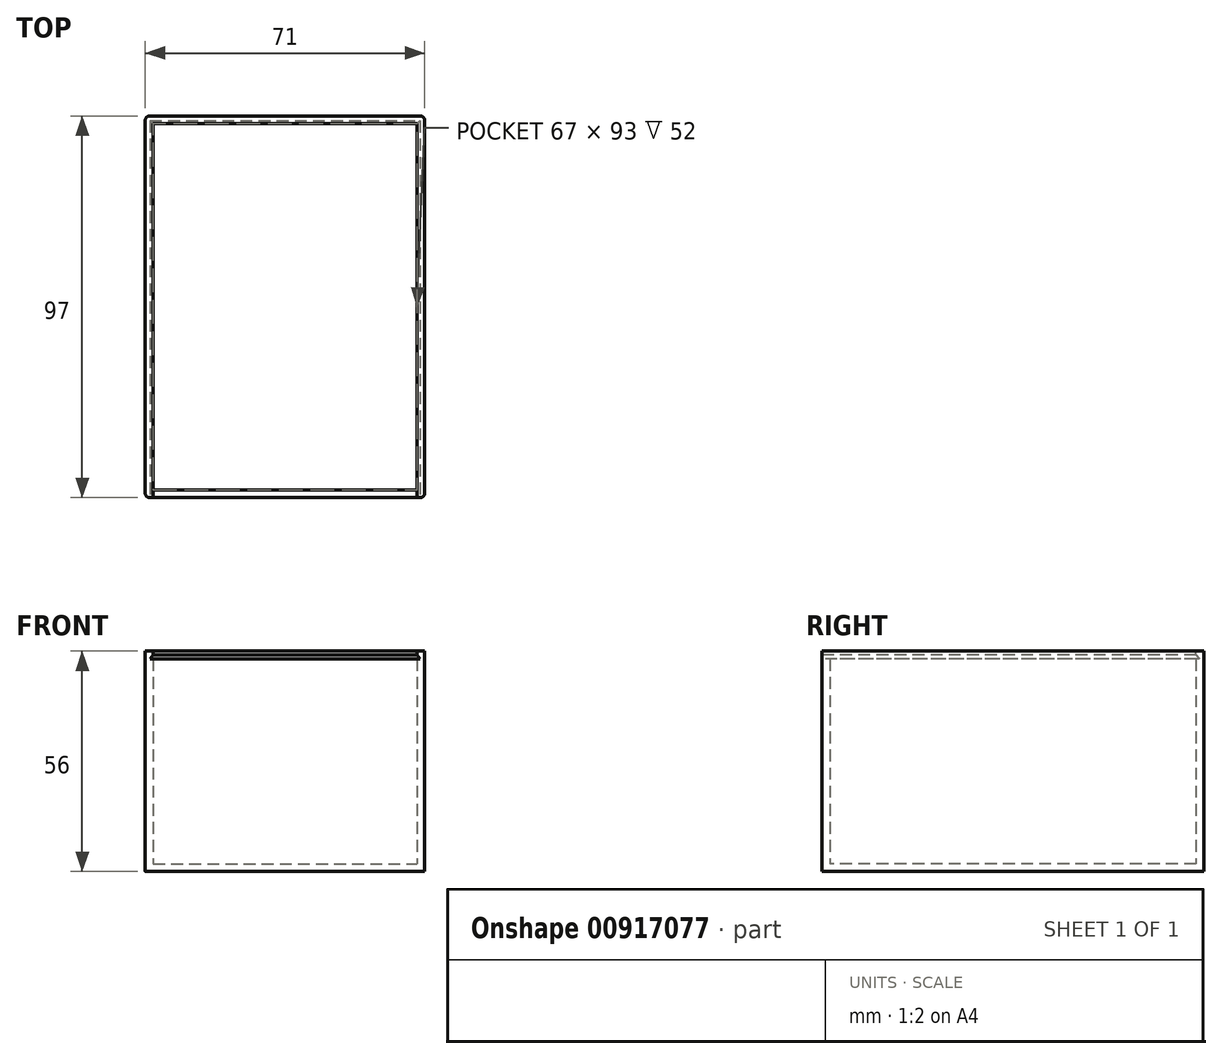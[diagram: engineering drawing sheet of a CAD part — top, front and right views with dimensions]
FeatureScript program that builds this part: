
annotation { "Feature Type Name" : "Feature", "Feature Type Description" : "" }
export const myFeature = defineFeature(function(context is Context, id is Id, definition is map)
    precondition{}
    {
        {
            var Q0;
            Q0=qCreatedBy(makeId("Front.planeOp"),FACE);
            var sketch = newSketch(context, id + "F0", { "sketchPlane" : qUnion([Q0])});
            skLineSegment(sketch, "E0.bottom", {"start": v(0, 0) * mm, "end": v(71, 0) * mm});
            skLineSegment(sketch, "E0.top", {"start": v(0, -54) * mm, "end": v(71, -54) * mm});
            skLineSegment(sketch, "E0.left", {"start": v(0, 0) * mm, "end": v(0, -54) * mm});
            skLineSegment(sketch, "E0.right", {"start": v(71, 0) * mm, "end": v(71, -54) * mm});
            skSolve(sketch);
        }
        {
            var Q0;
            Q0=qSketchRegion(id+"F0",true);
            extrude(context, id + "F1", {"entities" : qUnion([Q0]), "oppositeDirection" : true, "depth" : 97 * mm, "offsetDistance" : 25 * mm});
        }
        {
            var Q0;
            Q0=makeQuery(id+"F1.opExtrude","SWEPT_FACE",FACE,{"disambiguationData":[OSD([sQuery(id+"F0.wireOp",EDGE,"E0.bottom")])]});
            shell(context, id + "F2", {"entities" : qUnion([Q0]), "thickness" : 2 * mm});
        }
        {
            var Q0;
            Q0=makeQuery(id+"F1.opExtrude","CAP_FACE",FACE,{"disambiguationData":[OSD([sQuery(id+"F0.wireOp",EDGE,"E0.bottom"),sQuery(id+"F0.wireOp",EDGE,"E0.top"),sQuery(id+"F0.wireOp",EDGE,"E0.left"),sQuery(id+"F0.wireOp",EDGE,"E0.right")])],"isStart":true});
            var sketch = newSketch(context, id + "F3", { "sketchPlane" : qUnion([Q0])});
            skLineSegment(sketch, "E1", {"start": v(0, 0) * mm, "end": v(0, 2) * mm});
            skLineSegment(sketch, "E2", {"start": v(0, 2) * mm, "end": v(2, 2) * mm});
            skLineSegment(sketch, "E3", {"start": v(2, 2) * mm, "end": v(2, 1) * mm});
            skLineSegment(sketch, "E4", {"start": v(1.2, 0) * mm, "end": v(0, 0) * mm});
            skLineSegment(sketch, "E5", {"start": v(35.5, -54) * mm, "end": v(35.5, 0) * mm, "construction": true});
            skLineSegment(sketch, "E6", {"start": v(1.2, 0) * mm, "end": v(2, 1) * mm});
            skLineSegment(sketch, "E7.MirrorCS", {"start": v(69.8, 0) * mm, "end": v(69, 1) * mm});
            skLineSegment(sketch, "E8.MirrorCS", {"start": v(69, 2) * mm, "end": v(69, 1) * mm});
            skLineSegment(sketch, "E9.MirrorCS", {"start": v(69.8, 0) * mm, "end": v(71, 0) * mm});
            skLineSegment(sketch, "E10.MirrorCS", {"start": v(71, 0) * mm, "end": v(71, 2) * mm});
            skLineSegment(sketch, "E11.MirrorCS", {"start": v(71, 2) * mm, "end": v(69, 2) * mm});
            skSolve(sketch);
        }
        {
            var Q0;
            Q0=qSketchRegion(id+"F3",true);
            var Q1;
            Q1=makeQuery(id+"F1.opExtrude","CAP_FACE",FACE,{"disambiguationData":[OSD([sQuery(id+"F0.wireOp",EDGE,"E0.bottom"),sQuery(id+"F0.wireOp",EDGE,"E0.top"),sQuery(id+"F0.wireOp",EDGE,"E0.left"),sQuery(id+"F0.wireOp",EDGE,"E0.right")])],"isStart":false});
            extrude(context, id + "F4", {"entities" : qUnion([Q0]), "operationType" : NewBodyOperationType.ADD, "endBound" : BoundingType.UP_TO_SURFACE, "oppositeDirection" : true, "depth" : 25 * mm, "endBoundEntityFace" : qUnion([Q1]), "offsetDistance" : 25 * mm});
        }
        {
            var Q0;
            Q0=makeQuery(id+"F4.boolean.opBoolean","MERGE",FACE,{"derivedFrom":[makeQuery(id+"F1.opExtrude","SWEPT_FACE",FACE,{"disambiguationData":[OSD([sQuery(id+"F0.wireOp",EDGE,"E0.right")])]}),makeQuery(id+"F4.opExtrude","SWEPT_FACE",FACE,{"disambiguationData":[OSD([sQuery(id+"F3.wireOp",EDGE,"E10.MirrorCS")])]})]});
            var sketch = newSketch(context, id + "F5", { "sketchPlane" : qUnion([Q0])});
            skLineSegment(sketch, "E12", {"start": v(97, 2) * mm, "end": v(95, 2) * mm});
            skLineSegment(sketch, "E13", {"start": v(97, 0) * mm, "end": v(97, 2) * mm});
            skLineSegment(sketch, "E14", {"start": v(95, 2) * mm, "end": v(95, 1) * mm});
            skLineSegment(sketch, "E15", {"start": v(95, 1) * mm, "end": v(95.8, 0) * mm});
            skLineSegment(sketch, "E16", {"start": v(95.8, 0) * mm, "end": v(97, 0) * mm});
            skSolve(sketch);
        }
        {
            var Q0;
            Q0=makeQuery(id+"F5.imprint","IMPRINT",FACE,{"disambiguationData":[TD([[makeQuery(id+"F5.imprint","IMPRINT",EDGE,{"derivedFrom":sQuery(id+"F5.wireOp",EDGE,"E12")}),1.0]])]});
            var Q1;
            Q1=makeQuery(id+"F4.boolean.opBoolean","MERGE",FACE,{"derivedFrom":[makeQuery(id+"F1.opExtrude","SWEPT_FACE",FACE,{"disambiguationData":[OSD([sQuery(id+"F0.wireOp",EDGE,"E0.left")])]}),makeQuery(id+"F4.opExtrude","SWEPT_FACE",FACE,{"disambiguationData":[OSD([sQuery(id+"F3.wireOp",EDGE,"E1")])]})]});
            extrude(context, id + "F6", {"entities" : qUnion([Q0]), "operationType" : NewBodyOperationType.ADD, "endBound" : BoundingType.UP_TO_SURFACE, "oppositeDirection" : true, "depth" : 25 * mm, "endBoundEntityFace" : qUnion([Q1]), "offsetDistance" : 25 * mm});
        }
        {
            var Q0;
            Q0=makeQuery(id+"F4.boolean.opBoolean","MERGE",EDGE,{"derivedFrom":[makeQuery(id+"F1.opExtrude","CAP_EDGE",EDGE,{"disambiguationData":[OSD([sQuery(id+"F0.wireOp",EDGE,"E0.right")])],"isStart":true}),makeQuery(id+"F4.opExtrude","CAP_EDGE",EDGE,{"disambiguationData":[OSD([sQuery(id+"F3.wireOp",EDGE,"E10.MirrorCS")])],"isStart":true})]});
            var Q1;
            Q1=makeQuery(id+"F4.boolean.opBoolean","MERGE",EDGE,{"derivedFrom":[makeQuery(id+"F1.opExtrude","CAP_EDGE",EDGE,{"disambiguationData":[OSD([sQuery(id+"F0.wireOp",EDGE,"E0.right")])],"isStart":false}),makeQuery(id+"F4.opExtrude","CAP_EDGE",EDGE,{"disambiguationData":[OSD([sQuery(id+"F3.wireOp",EDGE,"E10.MirrorCS")])],"isStart":false})]});
            var Q2;
            Q2=makeQuery(id+"F4.boolean.opBoolean","MERGE",EDGE,{"derivedFrom":[makeQuery(id+"F1.opExtrude","CAP_EDGE",EDGE,{"disambiguationData":[OSD([sQuery(id+"F0.wireOp",EDGE,"E0.left")])],"isStart":true}),makeQuery(id+"F4.opExtrude","CAP_EDGE",EDGE,{"disambiguationData":[OSD([sQuery(id+"F3.wireOp",EDGE,"E1")])],"isStart":true})]});
            var Q3;
            Q3=makeQuery(id+"F4.boolean.opBoolean","MERGE",EDGE,{"derivedFrom":[makeQuery(id+"F1.opExtrude","CAP_EDGE",EDGE,{"disambiguationData":[OSD([sQuery(id+"F0.wireOp",EDGE,"E0.left")])],"isStart":false}),makeQuery(id+"F4.opExtrude","CAP_EDGE",EDGE,{"disambiguationData":[OSD([sQuery(id+"F3.wireOp",EDGE,"E1")])],"isStart":false})]});
            fillet(context, id + "F7", {"entities" : qUnion([Q0, Q1, Q2, Q3]), "radius" : 1.2 * mm, "tangentPropagation" : true, "allowEdgeOverflow" : false});
        }
    });
